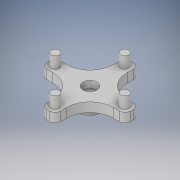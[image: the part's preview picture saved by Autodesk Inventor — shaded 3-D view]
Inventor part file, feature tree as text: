
AUTODESK INVENTOR PART (.ipt)
format: ipt  version: 2019 (Build 230136000, 136)  size: 207,872 bytes
history: native  units: in
note: dims shown in document units (in); Inventor stores cm internally (conversion verified against a paired STEP export)
features: extrude x7, sketch x5
ambient origin geometry x8: Origin, YZ Plane, XZ Plane, XY Plane, X Axis, Y Axis, Z Axis, Center Point
bodies: Solid1 (feature_tree)
feature tree (12):
  sketch  "Sketch1"  dims[d1=1.5748in d3=1.5748in d4=360.0deg d5=0.175in d6=360.0deg d7=0.125in d8=0.2in d9=0.0in d10=0.45in d11=0.0in]
  extrude  "Extrusion1"  Depth=0.45in TaperAngle=0.0deg
  extrude  "Extrusion2"  Depth=0.45in TaperAngle=360.0deg
  extrude  "Extrusion3"  Depth=0.45in TaperAngle=0.0deg
  extrude  "Extrusion4"  Depth=0.225in
  extrude  "Extrusion5"  Depth=0.3in
  extrude  "Extrusion6"  Depth=0.15in TaperAngle=0.0deg
  extrude  "Extrusion7"  Depth=0.25in
  sketch  "Sketch2"  dims[d12=0.45in d13=0.0in d14=1.5748in d16=360.0deg]
  sketch  "Sketch3"  dims[d18=0.225in d19=0.45in d20=0.0in]
  sketch  "Sketch4"  dims[d21=0.1in d22=0.225in]
  sketch  "Sketch5"  dims[d23=0.2in d24=0.0in d25=0.3in d26=0.15in d27=0.0in d28=0.25in d29=2.0in d30=0.0in]
